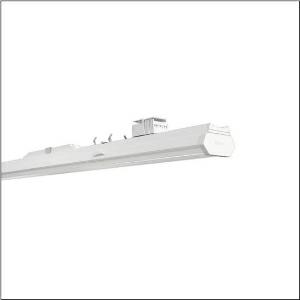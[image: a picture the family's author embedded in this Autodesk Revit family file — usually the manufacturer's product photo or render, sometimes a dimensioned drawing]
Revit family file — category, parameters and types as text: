
# Revit family: licross_r__21_performance_mo_52td16dn445g_3218
name_source: partatom
category: Lighting Fixtures
units: mm (PartAtom-declared; Revit-internal decimal feet)

## family parameters
Cut with Voids When Loaded = No
Host = Face
Light Source = No
Part Type = Normal
Room Calculation Point = No
Round Connector Dimension = Use Diameter
Shared = No

## types (1)
- --- (1 x LED, 4500 lm, 24.9 W, 4000K)
    Apparent Load = 25 VA
    CIE Flux Codes = 66 88 96 79 100
    Color Rendering = 80
    Color Temperature = 4000K
    Default Elevation = 1800 mm
    Description = Licross® 21 Performance MO, luminaire insert, of sheet steel, galvanised, coil coated, white, length: 1.500mm, width: 120mm, height: 123mm, LED rated luminous flux: 4.500lm, light colour: 840, control gear: DALI 2, control gear: ECG DALI, with plug, 5-pole, with phase selection, mains connection: 220..240V, AC, 50/60Hz, halogen-free wiring, primary light control with lens, of plastic, primary optical cover: cover, of PMMA, CAT 2 (L<= 3000cd/m²), light emission: direct/indirect distribution, primary light characteristic: symmetric, protection rating (complete): IP54, insulation class (complete): insulation class I (protective earthing), certification: CE, ENEC, VDE, UKCA, protection symbol: D if used in an environment with non-conductive dust loads with corresponding accessories, impact resistance: IK06, permissible ambient temperature for indoor applications: -25..+50°C, corresponds to IFS (International Featured Standards) requirements for safety and quality in the food industry, reducing of maximum allowable ambient temperature of 5°C with ceiling mounting, LABS conformity tested according to VDMA 24364:2018-05, packaging unit: 1 piece
    Height = 114 mm
    Lamp = 1 x LED
    Lamp Light Flux = 4500 lm
    Lamp Power = 24.9 W
    Lamp count = 1
    Length = 1500 mm
    Luminous efficacy = 181 lm/W
    Manufacturer = Siteco
    ModVariant = No
    Model = 52TD16DN445G
    Mounting Place = Ceiling
    Mounting Type = Pendant
    Number of Poles = 1
    OnlyDefault = Yes
    Power Factor = 1
    Product Name = Licross® 21 Performance MO
    Product group = luminaire insert
    ProductGroupID = 902
    Protection Class = Protection class I
    Protection Degree = IP 54
    RLX_Detail_Level = 1
    RlxData = <blob elided: 31501 chars, md5=6a774854>
    Socket = socket
    Standby Power = 0 W
    System Light Flux = 4500 lm
    System Power = 25 W
    Type Comments = factory setting: luminous flux: 100 % | dim-lin: 254 | 165 mA
    Type Image = l_1256148.jpg
    URL = http://relux.com
    VarID = @adj_039475
    Voltage = 0 V
    Weight = 0.00 kg
    Width = 120 mm

## geometry (parser evidence)
native form markers: Blend x4, Sweep x10
no freeform markers — native parametric forms only
